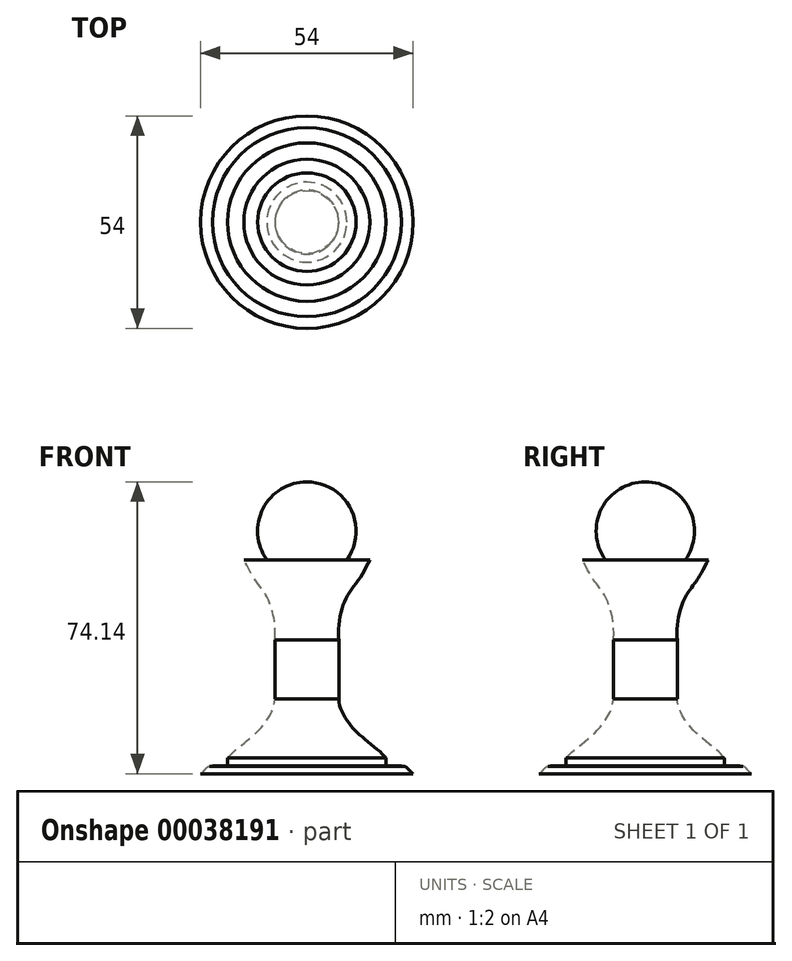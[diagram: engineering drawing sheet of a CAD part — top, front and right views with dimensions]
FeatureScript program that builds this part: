
annotation { "Feature Type Name" : "Feature", "Feature Type Description" : "" }
export const myFeature = defineFeature(function(context is Context, id is Id, definition is map)
    precondition{}
    {
        {
            var Q0;
            Q0=qCreatedBy(makeId("Front.planeOp"),FACE);
            var sketch = newSketch(context, id + "F0", { "sketchPlane" : qUnion([Q0])});
            skLineSegment(sketch, "E0", {"start": v(10.16, -3.03) * mm, "end": v(16, -3.03) * mm});
            skLineSegment(sketch, "E1", {"start": v(8.13, -23.4) * mm, "end": v(8.13, -38.4) * mm});
            skLineSegment(sketch, "E2", {"start": v(27, -57.4) * mm, "end": v(0, -57.4) * mm});
            skArc(sketch, "E3", {"start": v(10.16, -3.03) * mm, "mid": v(11.12, 9.96) * mm, "end": v(0, 16.75) * mm});
            skLineSegment(sketch, "E4", {"start": v(20.13, -55.4) * mm, "end": v(24, -55.4) * mm});
            skLineSegment(sketch, "E5", {"start": v(20.13, -53.4) * mm, "end": v(20.13, -55.4) * mm});
            skFitSpline(sketch, "E6", {"points": [v(24, -55.4) * mm, v(24.88, -55.58) * mm, v(25.67, -56.1) * mm, v(27, -57.4) * mm], "startDerivative": vector(2.08, -3.05) * mm, "endDerivative": vector(3.15, -1.58) * mm});
            skFitSpline(sketch, "E7", {"points": [v(8.13, -38.4) * mm, v(8.6, -40.94) * mm, v(9.92, -43.44) * mm, v(11.55, -45.7) * mm, v(13.33, -47.43) * mm, v(15.73, -49.48) * mm, v(18.62, -51.82) * mm, v(20.13, -53.4) * mm], "startDerivative": vector(2.15, -18.8) * mm, "endDerivative": vector(11.29, -11.76) * mm});
            skFitSpline(sketch, "E8", {"points": [v(16, -3.03) * mm, v(13.68, -7.33) * mm, v(11.1, -10.93) * mm, v(9.37, -14.23) * mm, v(8.22, -18.84) * mm, v(8.13, -23.4) * mm], "startDerivative": vector(-10.75, -20.3) * mm, "endDerivative": vector(2.15, -15.33) * mm});
            skPoint(sketch, "E9.orphan", {"position": v(0, -3.03) * mm});
            skPoint(sketch, "E10.end.orphan", {"position": v(0, -38.4) * mm});
            skPoint(sketch, "E11.orphan", {"position": v(0, -8.4) * mm});
            skPoint(sketch, "E12.orphan", {"position": v(0, -55.4) * mm});
            skLineSegment(sketch, "E13", {"start": v(0, 16.75) * mm, "end": v(0, -57.4) * mm});
            skSolve(sketch);
        }
        {
            var Q0;
            Q0 = qSketchRegion(id + "F0", true);
            var Q1;
            Q1=sQuery(id+"F0.wireOp",EDGE,"E13");
            revolve(context, id + "F1", {"entities" : qUnion([Q0]), "axis" : qUnion([Q1]), "revolveType" : RevolveType.FULL});
        }
    });
